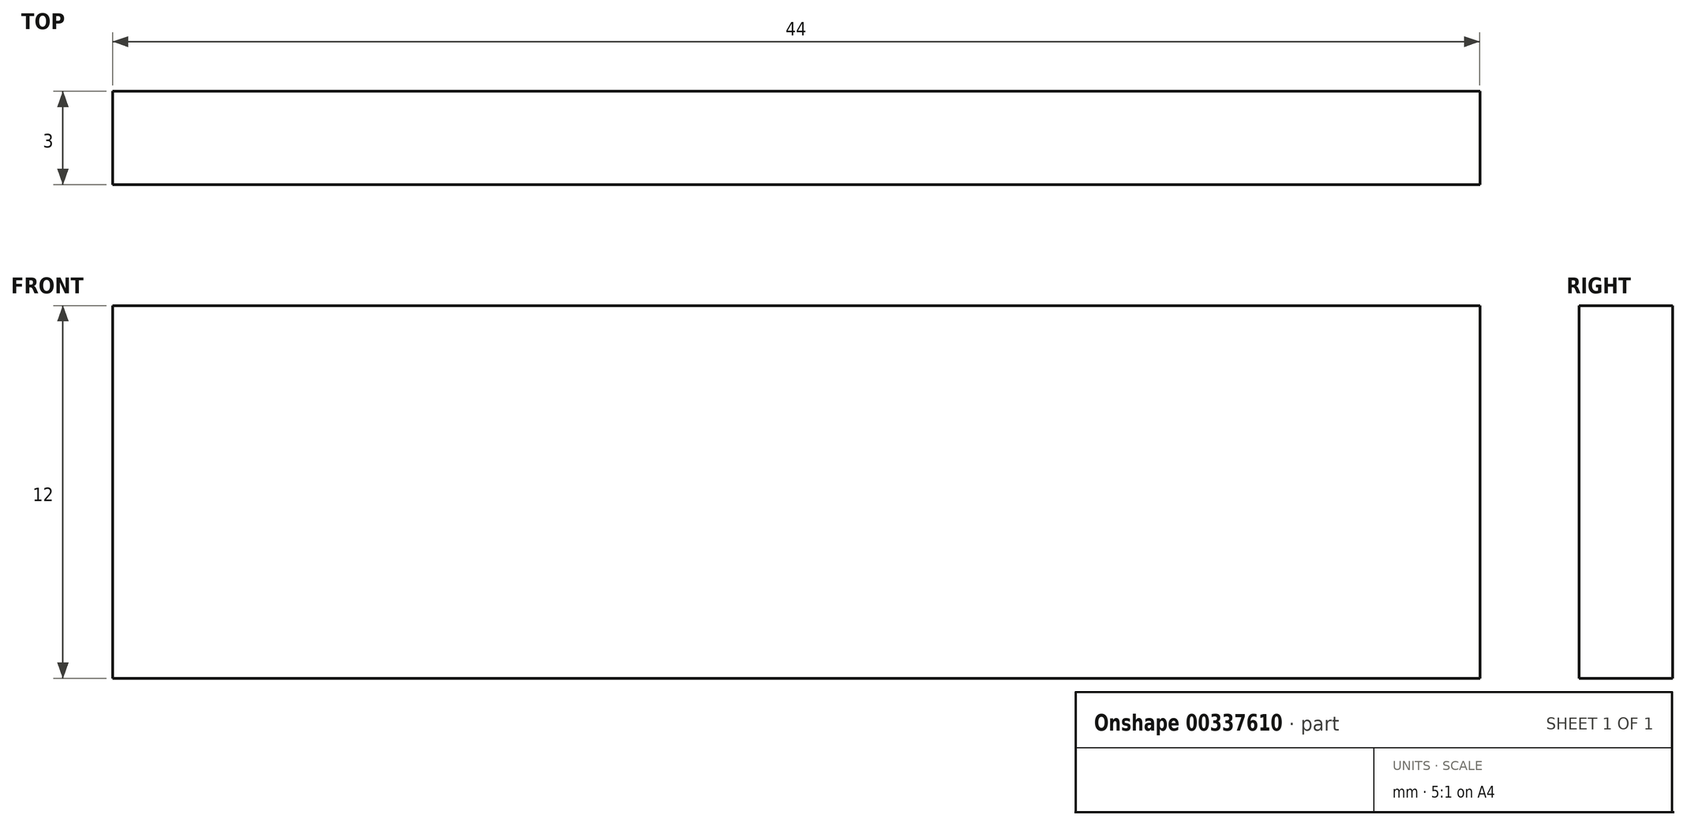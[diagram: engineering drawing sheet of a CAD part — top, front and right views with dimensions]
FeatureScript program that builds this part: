
annotation { "Feature Type Name" : "Feature", "Feature Type Description" : "" }
export const myFeature = defineFeature(function(context is Context, id is Id, definition is map)
    precondition{}
    {
        {
            var Q0;
            Q0=qCreatedBy(makeId("Front.planeOp"),FACE);
            var sketch = newSketch(context, id + "F0", { "sketchPlane" : qUnion([Q0])});
            skLineSegment(sketch, "E0", {"start": v(-21.73, 0) * mm, "end": v(-21.73, 12) * mm});
            skLineSegment(sketch, "E1", {"start": v(-21.73, 12) * mm, "end": v(22.27, 12) * mm});
            skLineSegment(sketch, "E2", {"start": v(22.27, 12) * mm, "end": v(22.27, 0) * mm});
            skLineSegment(sketch, "E3", {"start": v(22.27, 0) * mm, "end": v(-21.73, 0) * mm});
            skSolve(sketch);
        }
        {
            var Q0;
            Q0=makeQuery(id+"F0.imprint","IMPRINT",FACE,{"disambiguationData":[TD([[makeQuery(id+"F0.imprint","IMPRINT",EDGE,{"derivedFrom":sQuery(id+"F0.wireOp",EDGE,"E0")}),-1.0]])]});
            extrude(context, id + "F1", {"entities" : qUnion([Q0]), "endBound" : BoundingType.SYMMETRIC, "depth" : 3 * mm});
        }
    });
